# Revit family: Accessory-Soap_Dispenser-KOHLER-Bardon-K-5487T_1
name_source: partatom
category: Specialty Equipment
units: mm (PartAtom-declared; Revit-internal decimal feet)

## family parameters
Cut with Voids When Loaded = No
Host = Face
OmniClass Number = 23.31.25.29.13
OmniClass Title = Hand Soap Dispensers
Part Type = Normal
Room Calculation Point = No
Round Connector Dimension = Use Diameter
Shared = No

## types (1)
- CP-Polished Chrome
    ADA Compliant = No
    Assembly Code = C1030200
    Date Modified = 11/14/2024
    Default Elevation = 42"
    Description = Bardon Soap Dispenser
    Finish = Kohler-Plastic-CP-Polished_Chrome
    Height = 11 5/8"
    Length = 5 1/4"
    Manufacturer = Kohler Co.
    Master Format 2014 = 10 28 00
    Master Format 2014 Name = Toilet, Bath, and Laundry Accessories
    Material = Plastic
    Model = K-5487T-B-CP
    Product Name = Bardon
    Type = 1
    URL = http://www.kohler.com.cn
    WaterSense Certified = No
    Width = 4 11/16"

## geometry (parser evidence)
native form markers: Sweep x5
no freeform markers — native parametric forms only
